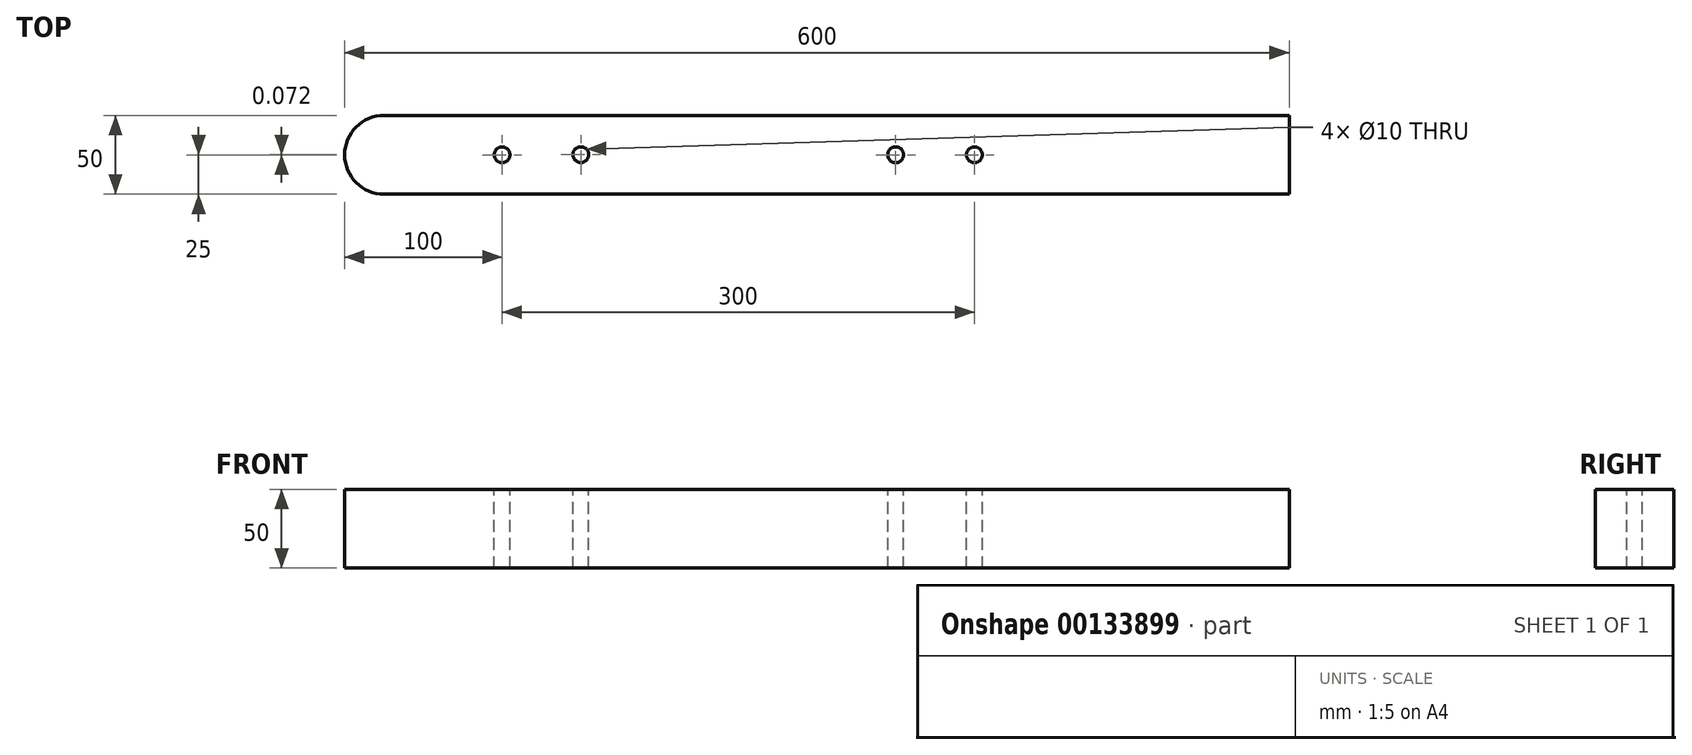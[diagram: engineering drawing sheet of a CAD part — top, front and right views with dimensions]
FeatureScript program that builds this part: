
annotation { "Feature Type Name" : "Feature", "Feature Type Description" : "" }
export const myFeature = defineFeature(function(context is Context, id is Id, definition is map)
    precondition{}
    {
        {
            var Q0;
            Q0=qCreatedBy(makeId("Front.planeOp"),FACE);
            var sketch = newSketch(context, id + "F0", { "sketchPlane" : qUnion([Q0])});
            skLineSegment(sketch, "E0.bottom", {"start": v(300, -14) * mm, "end": v(-300, -14) * mm});
            skLineSegment(sketch, "E0.top", {"start": v(300, 36) * mm, "end": v(-300, 36) * mm});
            skLineSegment(sketch, "E0.left", {"start": v(300, -14) * mm, "end": v(300, 36) * mm});
            skLineSegment(sketch, "E0.right", {"start": v(-300, -14) * mm, "end": v(-300, 36) * mm});
            skPoint(sketch, "E0.middle", {"position": v(0, 11) * mm});
            skSolve(sketch);
        }
        {
            var Q0;
            Q0=makeQuery(id+"F0.imprint","IMPRINT",FACE,{"disambiguationData":[TD([[makeQuery(id+"F0.imprint","IMPRINT",EDGE,{"derivedFrom":sQuery(id+"F0.wireOp",EDGE,"E0.bottom")}),-1.0]])]});
            extrude(context, id + "F1", {"entities" : qUnion([Q0]), "depth" : 50 * mm});
        }
        {
            var Q0;
            Q0=makeQuery(id+"F1.opExtrude","SWEPT_FACE",FACE,{"disambiguationData":[OSD([sQuery(id+"F0.wireOp",EDGE,"E0.top")])]});
            var sketch = newSketch(context, id + "F2", { "sketchPlane" : qUnion([Q0])});
            skCircle(sketch, "E1", {"center": v(-200, -25) * mm, "radius": 5 * mm});
            skPoint(sketch, "E1.centerSnap0", {"position": v(-300, -25) * mm});
            skCircle(sketch, "E2", {"center": v(-150, -24.93) * mm, "radius": 5 * mm});
            skCircle(sketch, "E3", {"center": v(50, -25) * mm, "radius": 5 * mm});
            skCircle(sketch, "E4", {"center": v(100, -25) * mm, "radius": 5 * mm});
            skSolve(sketch);
        }
        {
            var Q0;
            Q0=makeQuery(id+"F2.imprint","IMPRINT",FACE,{"disambiguationData":[TD([[makeQuery(id+"F2.imprint","IMPRINT",EDGE,{"derivedFrom":sQuery(id+"F2.wireOp",EDGE,"E3")}),1.0]])]});
            var Q1;
            Q1=makeQuery(id+"F2.imprint","IMPRINT",FACE,{"disambiguationData":[TD([[makeQuery(id+"F2.imprint","IMPRINT",EDGE,{"derivedFrom":sQuery(id+"F2.wireOp",EDGE,"E1")}),1.0]])]});
            var Q2;
            Q2=makeQuery(id+"F2.imprint","IMPRINT",FACE,{"disambiguationData":[TD([[makeQuery(id+"F2.imprint","IMPRINT",EDGE,{"derivedFrom":sQuery(id+"F2.wireOp",EDGE,"E4")}),1.0]])]});
            var Q3;
            Q3=makeQuery(id+"F2.imprint","IMPRINT",FACE,{"disambiguationData":[TD([[makeQuery(id+"F2.imprint","IMPRINT",EDGE,{"derivedFrom":sQuery(id+"F2.wireOp",EDGE,"E2")}),1.0]])]});
            extrude(context, id + "F3", {"entities" : qUnion([Q0, Q1, Q2, Q3]), "operationType" : NewBodyOperationType.REMOVE, "endBound" : BoundingType.THROUGH_ALL, "oppositeDirection" : true, "depth" : 25 * mm});
        }
        {
            var Q0;
            Q0=makeQuery(id+"F1.opExtrude","CAP_EDGE",EDGE,{"disambiguationData":[OSD([sQuery(id+"F0.wireOp",EDGE,"E0.right")])],"isStart":true});
            var Q1;
            Q1=makeQuery(id+"F1.opExtrude","CAP_EDGE",EDGE,{"disambiguationData":[OSD([sQuery(id+"F0.wireOp",EDGE,"E0.right")])],"isStart":false});
            fillet(context, id + "F4", {"entities" : qUnion([Q0, Q1]), "radius" : 25 * mm, "tangentPropagation" : true, "allowEdgeOverflow" : false});
        }
    });
